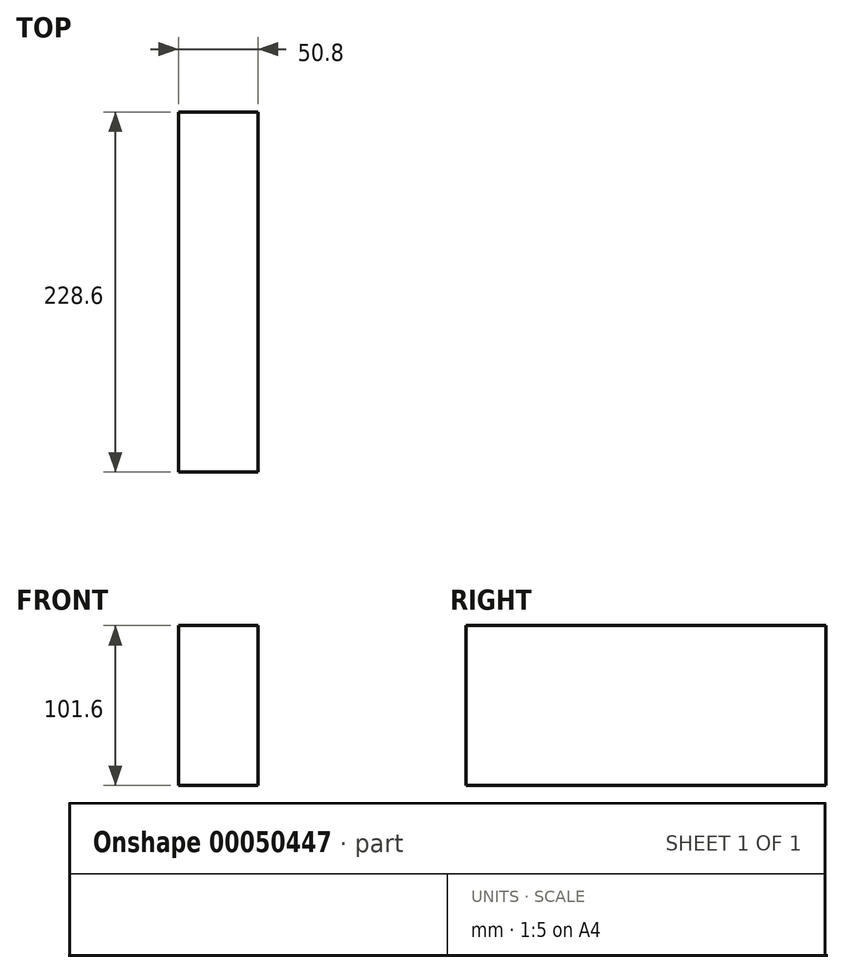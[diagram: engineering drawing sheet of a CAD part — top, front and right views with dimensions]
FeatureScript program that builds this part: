
annotation { "Feature Type Name" : "Feature", "Feature Type Description" : "" }
export const myFeature = defineFeature(function(context is Context, id is Id, definition is map)
    precondition{}
    {
        {
            var Q0;
            Q0=qCreatedBy(makeId("Front.planeOp"),FACE);
            var sketch = newSketch(context, id + "F0", { "sketchPlane" : qUnion([Q0])});
            skLineSegment(sketch, "E0.rect.bottom", {"start": v(-25.4, 50.8) * mm, "end": v(25.4, 50.8) * mm});
            skLineSegment(sketch, "E0.rect.top", {"start": v(-25.4, -50.8) * mm, "end": v(25.4, -50.8) * mm});
            skLineSegment(sketch, "E0.rect.left", {"start": v(-25.4, 50.8) * mm, "end": v(-25.4, -50.8) * mm});
            skLineSegment(sketch, "E0.rect.right", {"start": v(25.4, 50.8) * mm, "end": v(25.4, -50.8) * mm});
            skPoint(sketch, "E0.rect.middle", {"position": v(0, 0) * mm});
            skSolve(sketch);
        }
        {
            var Q0;
            Q0 = qSketchRegion(id + "F0", true);
            extrude(context, id + "F1", {"entities" : qUnion([Q0]), "endBound" : BoundingType.SYMMETRIC, "depth" : 228.6 * mm});
        }
    });
